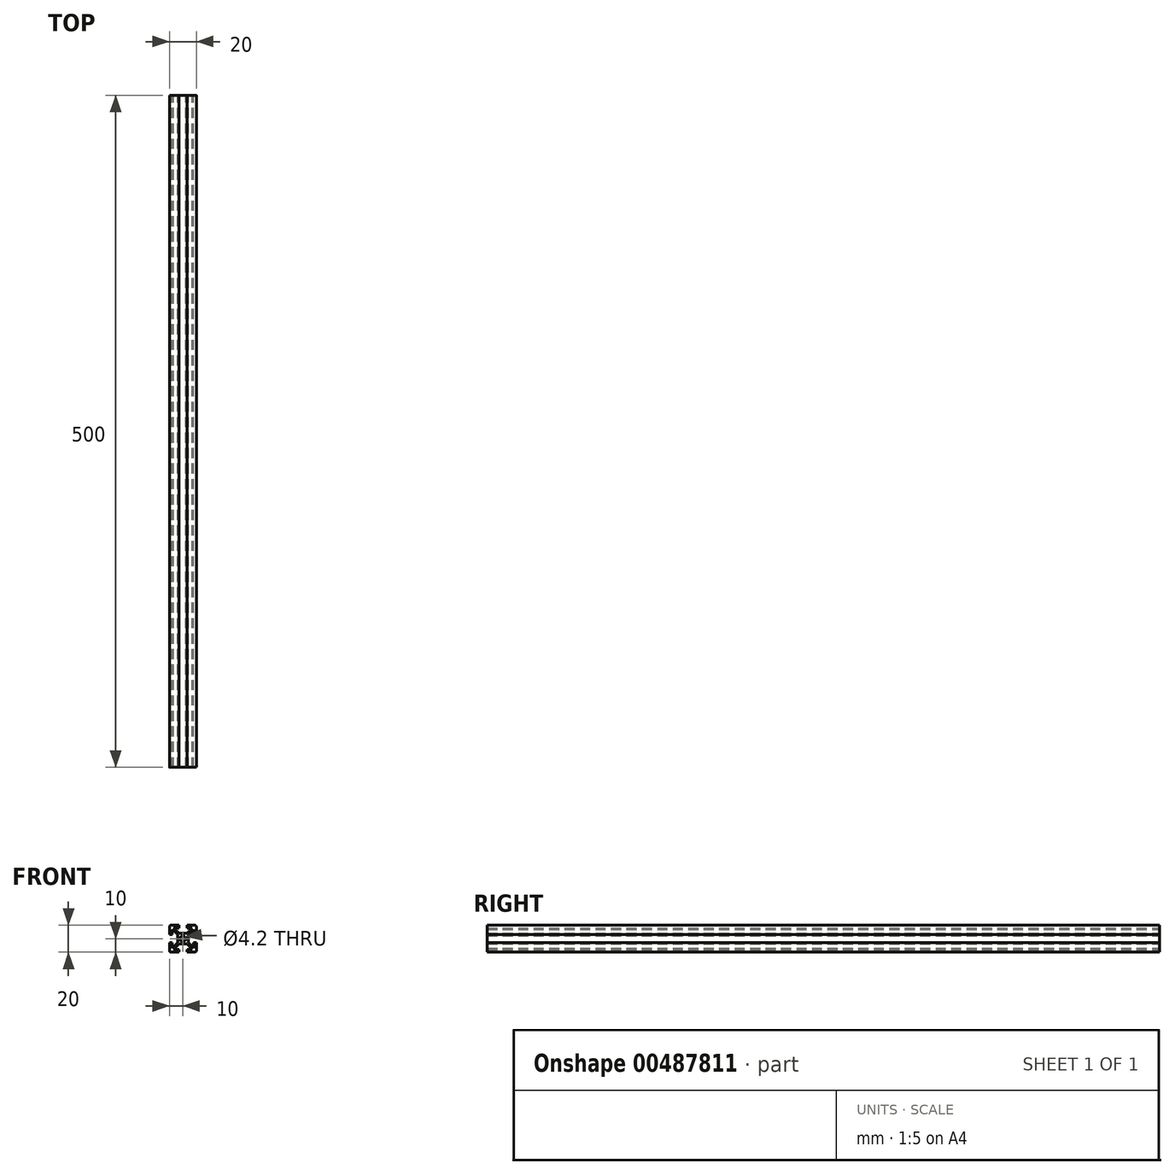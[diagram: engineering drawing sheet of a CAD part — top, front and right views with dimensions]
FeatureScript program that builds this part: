
annotation { "Feature Type Name" : "Feature", "Feature Type Description" : "" }
export const myFeature = defineFeature(function(context is Context, id is Id, definition is map)
    precondition{}
    {
        {
            var Q0;
            Q0=qCreatedBy(makeId("Front.planeOp"),FACE);
            var sketch = newSketch(context, id + "F0", { "sketchPlane" : qUnion([Q0])});
            skLineSegment(sketch, "E0.top", {"start": v(-9, -10) * mm, "end": v(-3, -10) * mm});
            skLineSegment(sketch, "E0.left", {"start": v(-10, 9) * mm, "end": v(-10, 3.08) * mm});
            skLineSegment(sketch, "E0.right", {"start": v(10, 9) * mm, "end": v(10, 3.08) * mm});
            skPoint(sketch, "E0.middle", {"position": v(0, 0) * mm});
            skArc(sketch, "E1.filletArc", {"start": v(-9, 10) * mm, "mid": v(-9.7, 9.7) * mm, "end": v(-10, 9) * mm});
            skArc(sketch, "E2.filletArc", {"start": v(10, 9) * mm, "mid": v(9.7, 9.7) * mm, "end": v(9, 10) * mm});
            skPoint(sketch, "E3.visualSharp", {"position": v(10, -10) * mm});
            skArc(sketch, "E3.filletArc", {"start": v(9, -10) * mm, "mid": v(9.7, -9.7) * mm, "end": v(10, -9) * mm});
            skArc(sketch, "E4.filletArc", {"start": v(-10, -9) * mm, "mid": v(-9.7, -9.7) * mm, "end": v(-9, -10) * mm});
            skCircle(sketch, "E5", {"center": v(0, 0) * mm, "radius": 2.1 * mm});
            skLineSegment(sketch, "E6.bottom", {"start": v(-3, 4) * mm, "end": v(3, 4) * mm});
            skLineSegment(sketch, "E6.top", {"start": v(-3, -4) * mm, "end": v(3, -4) * mm});
            skLineSegment(sketch, "E6.left", {"start": v(-4, 3) * mm, "end": v(-4, -3) * mm});
            skLineSegment(sketch, "E6.right", {"start": v(4, 3) * mm, "end": v(4, -3) * mm});
            skLineSegment(sketch, "E7", {"start": v(-4, 3) * mm, "end": v(-8, 7) * mm});
            skLineSegment(sketch, "E8", {"start": v(-7, 8) * mm, "end": v(-3, 4) * mm});
            skLineSegment(sketch, "E9", {"start": v(3, 4) * mm, "end": v(7, 8) * mm});
            skLineSegment(sketch, "E10", {"start": v(4, 3) * mm, "end": v(8, 7) * mm});
            skLineSegment(sketch, "E11", {"start": v(4, -3) * mm, "end": v(8, -7) * mm});
            skLineSegment(sketch, "E12", {"start": v(3, -4) * mm, "end": v(7, -8) * mm});
            skLineSegment(sketch, "E13", {"start": v(-3, -4) * mm, "end": v(-7, -8) * mm});
            skLineSegment(sketch, "E14", {"start": v(-8, -7) * mm, "end": v(-4, -3) * mm});
            skLineSegment(sketch, "E15.bottom", {"start": v(-7, 8) * mm, "end": v(-3, 8) * mm});
            skLineSegment(sketch, "E15.top", {"start": v(-7, -8) * mm, "end": v(-3, -8) * mm});
            skLineSegment(sketch, "E15.left", {"start": v(-8, 7) * mm, "end": v(-8, 3.18) * mm});
            skLineSegment(sketch, "E15.right", {"start": v(8, 7) * mm, "end": v(8, 3.08) * mm});
            skLineSegment(sketch, "E16", {"start": v(-3, -8) * mm, "end": v(-3, -10) * mm});
            skLineSegment(sketch, "E17", {"start": v(3, -8) * mm, "end": v(3, -10) * mm});
            skLineSegment(sketch, "E18", {"start": v(8, 3.08) * mm, "end": v(10, 3.08) * mm});
            skLineSegment(sketch, "E19", {"start": v(8, -3) * mm, "end": v(10, -3) * mm});
            skLineSegment(sketch, "E20", {"start": v(-3, 10) * mm, "end": v(-3, 8) * mm});
            skLineSegment(sketch, "E21", {"start": v(3, 10) * mm, "end": v(3, 8) * mm});
            skLineSegment(sketch, "E22", {"start": v(-10, 3.08) * mm, "end": v(-8.1, 3.08) * mm});
            skLineSegment(sketch, "E23", {"start": v(-10, -3) * mm, "end": v(-8, -3) * mm});
            skLineSegment(sketch, "E24.trimOffspring", {"start": v(-8, -3) * mm, "end": v(-8, -7) * mm});
            skLineSegment(sketch, "E25.trimOffspring", {"start": v(-10, -3) * mm, "end": v(-10, -9) * mm});
            skLineSegment(sketch, "E26.trimOffspring", {"start": v(3, 10) * mm, "end": v(9, 10) * mm});
            skLineSegment(sketch, "E27.trimOffspring", {"start": v(3, 8) * mm, "end": v(7, 8) * mm});
            skLineSegment(sketch, "E28", {"start": v(-9, 10) * mm, "end": v(-3, 10) * mm});
            skLineSegment(sketch, "E29.trimOffspring", {"start": v(10, -3) * mm, "end": v(10, -9) * mm});
            skLineSegment(sketch, "E30.trimOffspring", {"start": v(8, -3) * mm, "end": v(8, -7) * mm});
            skLineSegment(sketch, "E31.trimOffspring", {"start": v(3, -10) * mm, "end": v(9, -10) * mm});
            skLineSegment(sketch, "E32.trimOffspring", {"start": v(3, -8) * mm, "end": v(7, -8) * mm});
            skPoint(sketch, "E33.visualSharp", {"position": v(-8, 3.08) * mm});
            skArc(sketch, "E33.filletArc", {"start": v(-8.1, 3.08) * mm, "mid": v(-8.03, 3.1) * mm, "end": v(-8, 3.18) * mm});
            skSolve(sketch);
        }
        {
            assignVariable(context, id + "F1", {"name" : "x", "anyValue" : 500});
        }
        {
            var Q0;
            Q0=makeQuery(id+"F0.imprint","IMPRINT",FACE,{"disambiguationData":[TD([[makeQuery(id+"F0.imprint","IMPRINT",EDGE,{"derivedFrom":sQuery(id+"F0.wireOp",EDGE,"E0.top")}),1.0]])]});
            extrude(context, id + "F2", {"entities" : qUnion([Q0]), "depth" : (getVariable(context, 'x')) * mm, "offsetDistance" : 25 * mm});
        }
    });
